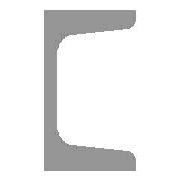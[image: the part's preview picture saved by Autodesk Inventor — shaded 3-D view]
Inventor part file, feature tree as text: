
AUTODESK INVENTOR PART (.ipt)
format: ipt  version: 2024 (Build 280153000, 153)  size: 135,168 bytes
history: native  units: mm (DEFAULTED — no unit token found)
features: other x3, extrude x1, sketch x1, plane x1
ambient origin geometry x8: Origin, YZ Plane, XZ Plane, XY Plane, X Axis, Y Axis, Z Axis, Center Point
bodies: Solid1 (feature_tree)
feature tree (6):
  other  "Driven Length"
  other  "Начальная плоскость"
  other  "Конечная плоскость"
  extrude  "Базовый элемент"  Depth=25.0mm
  sketch  "Sketch3"  dims[d0=5.0mm d1=25.0mm d2=38.0mm d3=7.0mm d4=19.0mm d5=1.52mm d6=30.0mm d7=0.0mm d23=7.0mm d24=3.5mm d25=0.0mm d26=-0.0mm d27=30.0mm d28=90.0deg d29=30.0mm]
  plane  "Work Plane3"
